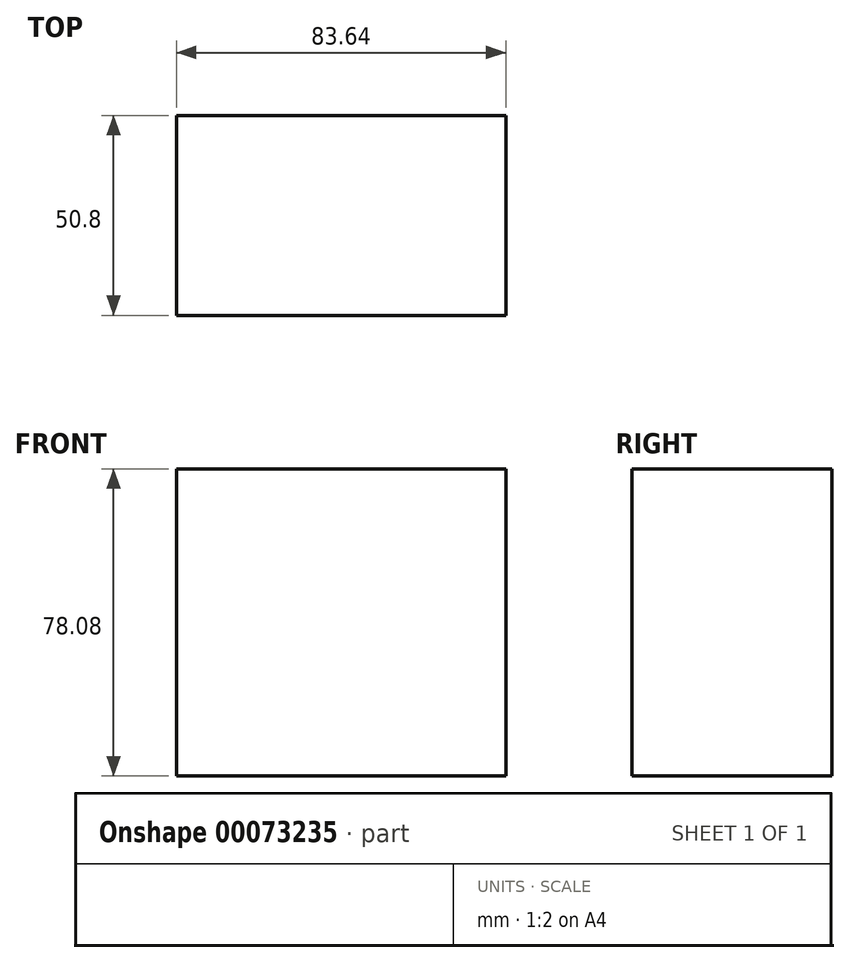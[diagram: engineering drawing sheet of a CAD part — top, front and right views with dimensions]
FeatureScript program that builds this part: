
annotation { "Feature Type Name" : "Feature", "Feature Type Description" : "" }
export const myFeature = defineFeature(function(context is Context, id is Id, definition is map)
    precondition{}
    {
        {
            var Q0;
            Q0=qCreatedBy(makeId("Front.planeOp"),FACE);
            var sketch = newSketch(context, id + "F1", { "sketchPlane" : qUnion([Q0])});
            skLineSegment(sketch, "E0.bottom", {"start": v(0, 0) * mm, "end": v(83.64, 0) * mm});
            skLineSegment(sketch, "E0.top", {"start": v(0, 78.08) * mm, "end": v(83.64, 78.08) * mm});
            skLineSegment(sketch, "E0.left", {"start": v(0, 0) * mm, "end": v(0, 78.08) * mm});
            skLineSegment(sketch, "E0.right", {"start": v(83.64, 0) * mm, "end": v(83.64, 78.08) * mm});
            skSolve(sketch);
        }
        {
            var Q0;
            Q0 = qSketchRegion(id + "F1", true);
            extrude(context, id + "F0", {"entities" : qUnion([Q0]), "depth" : 50.8 * mm});
        }
    });
